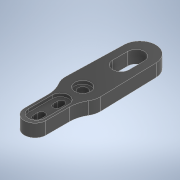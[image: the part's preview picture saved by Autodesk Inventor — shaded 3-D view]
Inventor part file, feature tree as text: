
AUTODESK INVENTOR PART (.ipt)
format: ipt  version: 2022.6 (Build 266554000, 554)  size: 199,680 bytes
history: native  units: mm
features: extrude x6, sketch x6, projected_geometry x1
ambient origin geometry x8: Origin, YZ Plane, XZ Plane, XY Plane, X Axis, Y Axis, Z Axis, Center Point
bodies: Solid1 (feature_tree)
feature tree (13):
  extrude  "Extrusion1"  Depth=3.0mm
  extrude  "Extrusion2"  Depth=4.0mm TaperAngle=0.0deg
  extrude  "Extrusion8"  Depth=5.2mm
  extrude  "Extrusion9"  TaperAngle=0.0deg  [1 undecoded]
  extrude  "Extrusion10"  Depth=3.4mm
  extrude  "Extrusion11"  Depth=1.0mm
  sketch  "Sketch1"  dims[d0=3.0mm d1=11.0mm]
  sketch  "Sketch2"  dims[d3=18.0mm d4=4.0mm d5=0.0mm]
  projected_geometry  "Projected Loop1"
  sketch  "Sketch8"  dims[d6=4.8mm d7=5.2mm]
  sketch  "Sketch10"  dims[d9=12.0mm d10=0.0mm d11=0.0mm]
  sketch  "Sketch11"  dims[d43=15.0mm d44=3.4mm]
  sketch  "Sketch12"  dims[d45=5.2mm d47=7.0mm d48=14.5mm d49=1.0mm d50=0.0mm d60=2.2mm d61=6.8mm d62=1.4mm d63=1.5mm d64=2.2mm d65=13.0mm d66=0.0mm d67=0.0mm d70=0.4mm d71=0.0mm d72=5.5mm d73=8.5mm d74=10.0mm d75=5.0mm d76=1.0mm d77=0.0mm d78=0.2mm d79=7.5mm]
note: 1 required parameter value undecoded (feature->parameter linkage not recoverable at this tier; creation-order binding heuristic only, values carry confidence <= 0.55)
